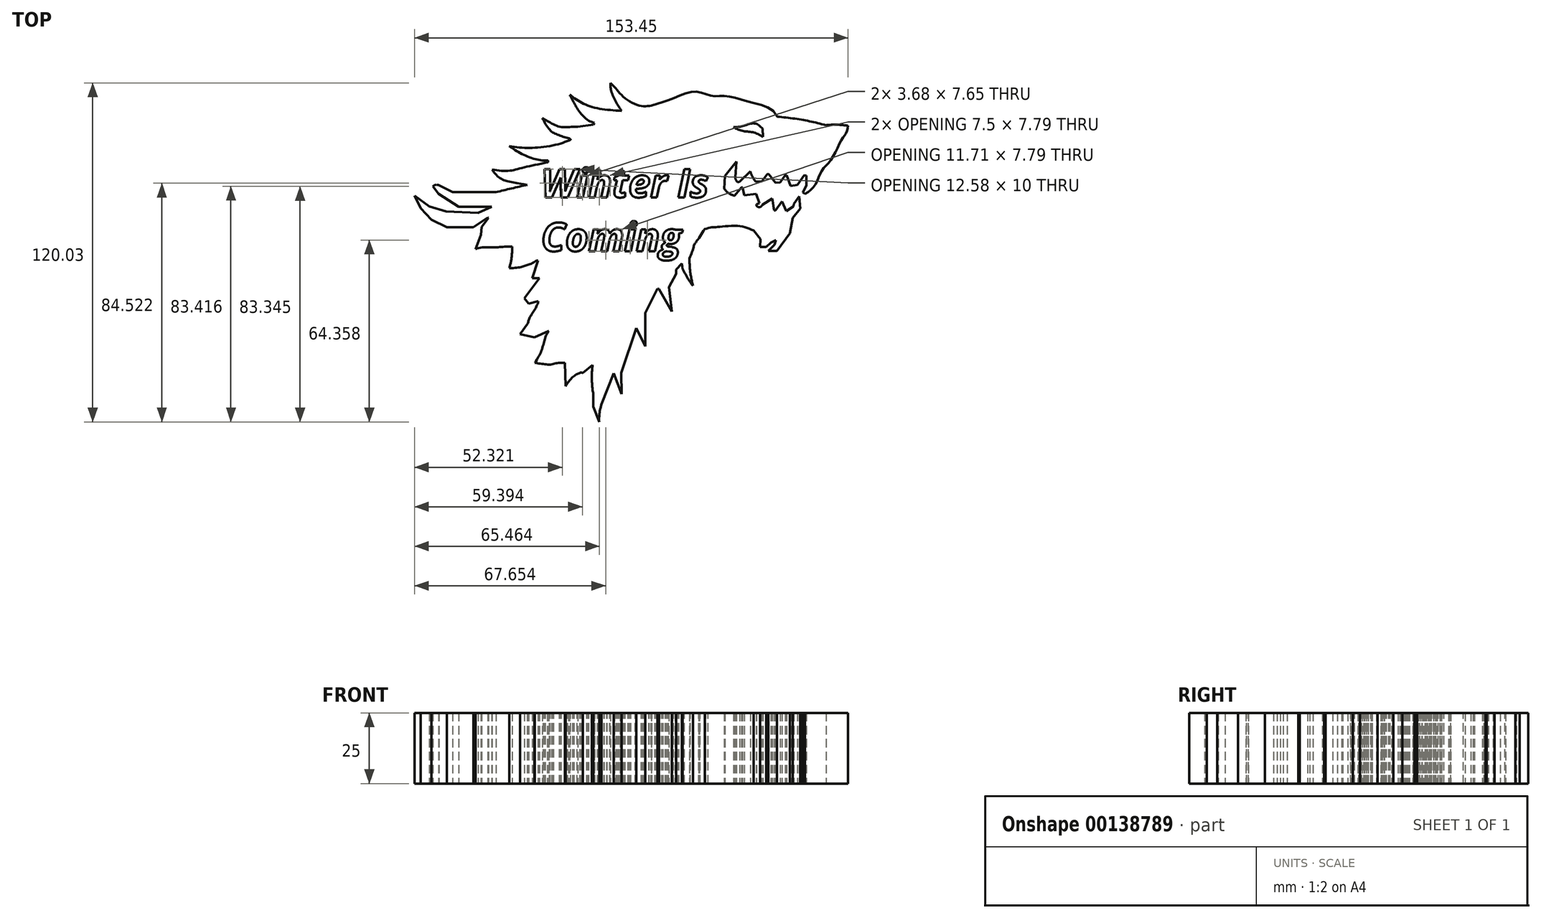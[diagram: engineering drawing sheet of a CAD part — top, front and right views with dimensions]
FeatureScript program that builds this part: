
annotation { "Feature Type Name" : "Feature", "Feature Type Description" : "" }
export const myFeature = defineFeature(function(context is Context, id is Id, definition is map)
    precondition{}
    {
        {
            var Q0;
            Q0=qCreatedBy(makeId("Top.planeOp"),FACE);
            var sketch = newSketch(context, id + "F0", { "sketchPlane" : qUnion([Q0])});
            skLineSegment(sketch, "E0", {"start": v(0, -46.34) * mm, "end": v(0, 97.64) * mm, "construction": true});
            skLineSegment(sketch, "E1", {"start": v(-98.9, 0) * mm, "end": v(160.67, 0) * mm, "construction": true});
            skFitSpline(sketch, "E2", {"points": [v(8.37, 46.02) * mm, v(16.5, 48.73) * mm, v(24.2, 50.9) * mm, v(29.67, 49.45) * mm, v(34.86, 49.36) * mm, v(43.4, 47.27) * mm, v(53, 42.06) * mm], "startDerivative": vector(47.53, 12.6) * mm, "endDerivative": vector(25.31, -53.78) * mm});
            skFitSpline(sketch, "E3", {"points": [v(53, 42.06) * mm, v(61.93, 40.92) * mm, v(70.2, 39.06) * mm], "startDerivative": vector(17.28, -1.4) * mm, "endDerivative": vector(17.12, -4.59) * mm});
            skFitSpline(sketch, "E4", {"points": [v(70.2, 39.06) * mm, v(73.91, 39.25) * mm, v(78, 38.88) * mm], "startDerivative": vector(7.53, 0.65) * mm, "endDerivative": vector(8.07, -1) * mm});
            skFitSpline(sketch, "E5", {"points": [v(78, 38.88) * mm, v(77.15, 36.05) * mm, v(75.57, 33.69) * mm, v(71.82, 26.58) * mm, v(68.71, 23.01) * mm, v(66.37, 17.92) * mm, v(62.79, 14.7) * mm], "startDerivative": vector(-2.44, -23.85) * mm, "endDerivative": vector(-25.04, -14.1) * mm});
            skLineSegment(sketch, "E6", {"start": v(62.79, 14.7) * mm, "end": v(62, 15.24) * mm});
            skLineSegment(sketch, "E7", {"start": v(62, 15.24) * mm, "end": v(63.2, 17.7) * mm});
            skLineSegment(sketch, "E8", {"start": v(63.2, 17.7) * mm, "end": v(63.2, 21.18) * mm});
            skLineSegment(sketch, "E9", {"start": v(63.2, 21.18) * mm, "end": v(62.45, 21.32) * mm});
            skLineSegment(sketch, "E10", {"start": v(62.45, 21.32) * mm, "end": v(60.09, 17.98) * mm});
            skLineSegment(sketch, "E11", {"start": v(60.09, 17.98) * mm, "end": v(57.72, 17.51) * mm});
            skLineSegment(sketch, "E12", {"start": v(57.72, 17.51) * mm, "end": v(56.32, 21.32) * mm});
            skLineSegment(sketch, "E13", {"start": v(56.32, 21.32) * mm, "end": v(55.78, 21.31) * mm});
            skLineSegment(sketch, "E14", {"start": v(55.78, 21.31) * mm, "end": v(54.02, 18.83) * mm});
            skLineSegment(sketch, "E15", {"start": v(54.02, 18.83) * mm, "end": v(52.38, 18.64) * mm});
            skLineSegment(sketch, "E16", {"start": v(52.38, 18.64) * mm, "end": v(49.96, 21.76) * mm});
            skLineSegment(sketch, "E17", {"start": v(49.96, 21.76) * mm, "end": v(49.36, 21.76) * mm});
            skLineSegment(sketch, "E18", {"start": v(49.36, 21.76) * mm, "end": v(47.55, 19.25) * mm});
            skLineSegment(sketch, "E19", {"start": v(47.55, 19.25) * mm, "end": v(45.5, 19.02) * mm});
            skFitSpline(sketch, "E20", {"points": [v(45.5, 19.02) * mm, v(44.43, 20.33) * mm, v(43.4, 22.76) * mm], "startDerivative": vector(-3.09, 1.68) * mm, "endDerivative": vector(-1.4, 5.58) * mm});
            skLineSegment(sketch, "E21", {"start": v(43.4, 22.76) * mm, "end": v(39.6, 19.05) * mm});
            skLineSegment(sketch, "E22", {"start": v(38.55, 26.15) * mm, "end": v(38.05, 20.53) * mm});
            skFitSpline(sketch, "E23", {"points": [v(38.05, 20.53) * mm, v(38.32, 19.7) * mm, v(38.9, 18.95) * mm, v(39.6, 19.05) * mm], "startDerivative": vector(0.59, -2.33) * mm, "endDerivative": vector(2.36, 0.9) * mm});
            skLineSegment(sketch, "E24", {"start": v(38.55, 26.15) * mm, "end": v(34.4, 21.11) * mm});
            skLineSegment(sketch, "E25", {"start": v(34.4, 21.11) * mm, "end": v(34.15, 16.58) * mm});
            skFitSpline(sketch, "E26", {"points": [v(34.15, 16.58) * mm, v(35.74, 14.98) * mm, v(37.83, 14.05) * mm], "startDerivative": vector(3.39, -3.5) * mm, "endDerivative": vector(3.98, -1.53) * mm});
            skLineSegment(sketch, "E27", {"start": v(37.83, 14.05) * mm, "end": v(40.2, 16.98) * mm});
            skLineSegment(sketch, "E28", {"start": v(40.2, 16.98) * mm, "end": v(40.7, 16.98) * mm});
            skLineSegment(sketch, "E29", {"start": v(40.7, 16.98) * mm, "end": v(41.3, 14.23) * mm});
            skLineSegment(sketch, "E30", {"start": v(41.3, 14.23) * mm, "end": v(45.53, 14.8) * mm});
            skLineSegment(sketch, "E31", {"start": v(45.53, 14.8) * mm, "end": v(46.61, 11.43) * mm});
            skLineSegment(sketch, "E32", {"start": v(46.61, 11.43) * mm, "end": v(45.6, 11.1) * mm});
            skLineSegment(sketch, "E33", {"start": v(47.71, 10.9) * mm, "end": v(51.18, 13.14) * mm});
            skFitSpline(sketch, "E34", {"points": [v(47.71, 10.9) * mm, v(47.14, 10.2) * mm, v(45.87, 10.24) * mm, v(45.6, 11.1) * mm], "startDerivative": vector(-1.25, -2.64) * mm, "endDerivative": vector(-0.16, 3.24) * mm});
            skLineSegment(sketch, "E35", {"start": v(51.18, 13.14) * mm, "end": v(51.76, 8.96) * mm});
            skLineSegment(sketch, "E36", {"start": v(51.76, 8.96) * mm, "end": v(52.35, 8.96) * mm});
            skLineSegment(sketch, "E37", {"start": v(52.35, 8.96) * mm, "end": v(54.64, 12.02) * mm});
            skLineSegment(sketch, "E38", {"start": v(54.64, 12.02) * mm, "end": v(56.15, 8.66) * mm});
            skLineSegment(sketch, "E39", {"start": v(56.15, 8.66) * mm, "end": v(58.7, 10.29) * mm});
            skLineSegment(sketch, "E40", {"start": v(58.7, 10.29) * mm, "end": v(58.8, 11.25) * mm});
            skLineSegment(sketch, "E41", {"start": v(58.8, 11.25) * mm, "end": v(60.75, 13.83) * mm});
            skLineSegment(sketch, "E42", {"start": v(60.75, 13.83) * mm, "end": v(61.12, 9.51) * mm});
            skLineSegment(sketch, "E43", {"start": v(61.12, 9.51) * mm, "end": v(58.37, 6.23) * mm});
            skLineSegment(sketch, "E44", {"start": v(58.37, 6.23) * mm, "end": v(57.38, 0.75) * mm});
            skLineSegment(sketch, "E45", {"start": v(57.38, 0.75) * mm, "end": v(52.78, -5.5) * mm});
            skLineSegment(sketch, "E46", {"start": v(52.78, -5.5) * mm, "end": v(49.73, -5.5) * mm});
            skLineSegment(sketch, "E47", {"start": v(49.73, -5.5) * mm, "end": v(52, -3.3) * mm});
            skLineSegment(sketch, "E48", {"start": v(52, -3.3) * mm, "end": v(52.42, -1.58) * mm});
            skLineSegment(sketch, "E49", {"start": v(52.42, -1.58) * mm, "end": v(50.65, -2.56) * mm});
            skLineSegment(sketch, "E50", {"start": v(50.65, -2.56) * mm, "end": v(49.07, -4.09) * mm});
            skLineSegment(sketch, "E51", {"start": v(49.07, -4.09) * mm, "end": v(46.86, -4.09) * mm});
            skLineSegment(sketch, "E52", {"start": v(46.86, -4.09) * mm, "end": v(47.02, -1.26) * mm});
            skLineSegment(sketch, "E53", {"start": v(47.02, -1.26) * mm, "end": v(44.6, 1.8) * mm});
            skFitSpline(sketch, "E54", {"points": [v(44.6, 1.8) * mm, v(38.62, 3.43) * mm, v(31.22, 2.96) * mm, v(30.22, 2.96) * mm, v(27.26, 2.3) * mm], "startDerivative": vector(-17, 7.19) * mm, "endDerivative": vector(-16.02, -4.1) * mm});
            skFitSpline(sketch, "E55", {"points": [v(27.26, 2.3) * mm, v(24.24, -2.27) * mm, v(23.71, -3.01) * mm, v(23.18, -4.49) * mm, v(21.86, -8.07) * mm], "startDerivative": vector(-9.48, -15.13) * mm, "endDerivative": vector(-7.44, -13.5) * mm});
            skFitSpline(sketch, "E56", {"points": [v(21.86, -8.07) * mm, v(22.1, -12.6) * mm, v(23.06, -17.73) * mm], "startDerivative": vector(0.3, -9.94) * mm, "endDerivative": vector(2.15, -9.73) * mm});
            skLineSegment(sketch, "E57", {"start": v(19.14, -9.9) * mm, "end": v(19.48, -11.87) * mm});
            skFitSpline(sketch, "E58", {"points": [v(19.48, -11.87) * mm, v(20.92, -14.56) * mm, v(23.06, -17.73) * mm], "startDerivative": vector(3.02, -5.51) * mm, "endDerivative": vector(4.86, -6.04) * mm});
            skLineSegment(sketch, "E59", {"start": v(19.14, -9.9) * mm, "end": v(17.18, -12.06) * mm});
            skLineSegment(sketch, "E60", {"start": v(17.18, -12.06) * mm, "end": v(17.18, -13.56) * mm});
            skLineSegment(sketch, "E61", {"start": v(17.18, -13.56) * mm, "end": v(14.64, -18.29) * mm});
            skLineSegment(sketch, "E62", {"start": v(14.64, -18.29) * mm, "end": v(15.58, -26.93) * mm});
            skLineSegment(sketch, "E63", {"start": v(15.58, -26.93) * mm, "end": v(11.12, -18.85) * mm});
            skLineSegment(sketch, "E64", {"start": v(11.12, -18.85) * mm, "end": v(10.6, -18.76) * mm});
            skLineSegment(sketch, "E65", {"start": v(10.6, -18.76) * mm, "end": v(6.22, -27.44) * mm});
            skLineSegment(sketch, "E66", {"start": v(6.22, -27.44) * mm, "end": v(6.17, -39.18) * mm});
            skLineSegment(sketch, "E67", {"start": v(6.17, -39.18) * mm, "end": v(3.07, -32.74) * mm});
            skLineSegment(sketch, "E68", {"start": v(3.07, -32.74) * mm, "end": v(-2.3, -48.66) * mm});
            skLineSegment(sketch, "E69", {"start": v(-2.3, -48.66) * mm, "end": v(-2.17, -56.06) * mm});
            skLineSegment(sketch, "E70", {"start": v(-2.17, -56.06) * mm, "end": v(-4.99, -48.79) * mm});
            skLineSegment(sketch, "E71", {"start": v(-4.99, -48.79) * mm, "end": v(-9.28, -59.71) * mm});
            skFitSpline(sketch, "E72", {"points": [v(-9.28, -59.71) * mm, v(-9.83, -61.89) * mm, v(-10.04, -63.68) * mm, v(-10.08, -65.99) * mm], "startDerivative": vector(-1.5, -7.23) * mm, "endDerivative": vector(0.61, -9.45) * mm});
            skLineSegment(sketch, "E73", {"start": v(-10.08, -65.99) * mm, "end": v(-12.22, -60.51) * mm});
            skLineSegment(sketch, "E74", {"start": v(-12.22, -60.51) * mm, "end": v(-12.22, -55.67) * mm});
            skFitSpline(sketch, "E75", {"points": [v(-12.22, -55.67) * mm, v(-12.62, -52.29) * mm, v(-12.62, -47.83) * mm, v(-12.44, -45.9) * mm], "startDerivative": vector(-2.35, 9.95) * mm, "endDerivative": vector(0.6, 6.7) * mm});
            skLineSegment(sketch, "E76", {"start": v(-12.44, -45.9) * mm, "end": v(-15.86, -48.6) * mm});
            skFitSpline(sketch, "E77", {"points": [v(-15.86, -48.6) * mm, v(-16.85, -48.6) * mm, v(-19.68, -50.34) * mm, v(-21.96, -53.33) * mm], "startDerivative": vector(-4.67, 0.75) * mm, "endDerivative": vector(-4.96, -8.28) * mm});
            skLineSegment(sketch, "E78", {"start": v(-21.96, -53.33) * mm, "end": v(-22.2, -45.03) * mm});
            skFitSpline(sketch, "E79", {"points": [v(-22.2, -45.03) * mm, v(-23.7, -45.03) * mm, v(-25.38, -45.24) * mm, v(-27.7, -45.69) * mm, v(-30.45, -45.39) * mm, v(-32.84, -45.03) * mm], "startDerivative": vector(-10.12, -0.25) * mm, "endDerivative": vector(-8.12, 2.64) * mm});
            skFitSpline(sketch, "E80", {"points": [v(-32.84, -45.03) * mm, v(-30.46, -40.57) * mm, v(-29.33, -36.68) * mm, v(-27.93, -33.79) * mm], "startDerivative": vector(7.96, 12) * mm, "endDerivative": vector(7.34, 9.15) * mm});
            skLineSegment(sketch, "E81", {"start": v(-27.93, -33.79) * mm, "end": v(-33, -36.1) * mm});
            skLineSegment(sketch, "E82", {"start": v(-33, -36.1) * mm, "end": v(-38.14, -34.9) * mm});
            skLineSegment(sketch, "E83", {"start": v(-38.14, -34.9) * mm, "end": v(-35.38, -31.25) * mm});
            skFitSpline(sketch, "E84", {"points": [v(-35.38, -31.25) * mm, v(-34.63, -29.02) * mm, v(-32.62, -25.74) * mm, v(-31.58, -23.28) * mm], "startDerivative": vector(1.7, 7.16) * mm, "endDerivative": vector(2.6, 7.43) * mm});
            skLineSegment(sketch, "E85", {"start": v(-31.58, -23.28) * mm, "end": v(-35.08, -24.1) * mm});
            skLineSegment(sketch, "E86", {"start": v(-35.08, -24.1) * mm, "end": v(-36.57, -22.16) * mm});
            skLineSegment(sketch, "E87", {"start": v(-36.57, -22.16) * mm, "end": v(-31.2, -15.15) * mm});
            skLineSegment(sketch, "E88", {"start": v(-31.2, -15.15) * mm, "end": v(-33.74, -15.15) * mm});
            skLineSegment(sketch, "E89", {"start": v(-33.74, -15.15) * mm, "end": v(-31.79, -8.9) * mm});
            skFitSpline(sketch, "E90", {"points": [v(-31.79, -8.9) * mm, v(-33.97, -9.91) * mm, v(-36.14, -10.62) * mm, v(-38.4, -11.28) * mm, v(-41.9, -11.6) * mm], "startDerivative": vector(-6.1, 1.36) * mm, "endDerivative": vector(-8.76, -0.8) * mm});
            skFitSpline(sketch, "E91", {"points": [v(-41.9, -11.6) * mm, v(-41.13, -8.29) * mm, v(-40.83, -3.95) * mm], "startDerivative": vector(1.85, 6.75) * mm, "endDerivative": vector(0.43, 8.1) * mm});
            skFitSpline(sketch, "E92", {"points": [v(-40.83, -3.95) * mm, v(-45.11, -4.06) * mm, v(-48.54, -4.17) * mm, v(-53.9, -4.78) * mm], "startDerivative": vector(-10.76, 1.27) * mm, "endDerivative": vector(-11.93, -6.43) * mm});
            skLineSegment(sketch, "E93", {"start": v(-53.9, -4.78) * mm, "end": v(-51.88, 0.27) * mm});
            skLineSegment(sketch, "E94", {"start": v(-51.88, 0.27) * mm, "end": v(-51.63, 3.08) * mm});
            skLineSegment(sketch, "E95", {"start": v(-51.63, 3.08) * mm, "end": v(-49.22, 6.21) * mm});
            skLineSegment(sketch, "E96", {"start": v(-49.22, 6.21) * mm, "end": v(-49.5, 6.43) * mm});
            skLineSegment(sketch, "E97", {"start": v(-49.5, 6.43) * mm, "end": v(-54.64, 2.98) * mm});
            skLineSegment(sketch, "E98", {"start": v(-54.64, 2.98) * mm, "end": v(-63.96, 2.98) * mm});
            skLineSegment(sketch, "E99", {"start": v(-63.96, 2.98) * mm, "end": v(-69.48, 5.65) * mm});
            skLineSegment(sketch, "E100", {"start": v(-69.48, 5.65) * mm, "end": v(-73.26, 9.73) * mm});
            skLineSegment(sketch, "E101", {"start": v(-73.26, 9.73) * mm, "end": v(-75.45, 14.1) * mm});
            skLineSegment(sketch, "E102", {"start": v(-75.45, 14.1) * mm, "end": v(-70.28, 10.27) * mm});
            skLineSegment(sketch, "E103", {"start": v(-70.28, 10.27) * mm, "end": v(-64.26, 8.53) * mm});
            skLineSegment(sketch, "E104", {"start": v(-64.26, 8.53) * mm, "end": v(-52.92, 7.99) * mm});
            skLineSegment(sketch, "E105", {"start": v(-52.92, 7.99) * mm, "end": v(-48.15, 10.22) * mm});
            skLineSegment(sketch, "E106", {"start": v(-48.15, 10.22) * mm, "end": v(-59.86, 10.22) * mm});
            skLineSegment(sketch, "E107", {"start": v(-59.86, 10.22) * mm, "end": v(-66.87, 14.75) * mm});
            skLineSegment(sketch, "E108", {"start": v(-66.87, 14.75) * mm, "end": v(-68.94, 17.44) * mm});
            skLineSegment(sketch, "E109", {"start": v(-66.8, 17.83) * mm, "end": v(-62.02, 15.35) * mm});
            skLineSegment(sketch, "E110", {"start": v(-62.02, 15.35) * mm, "end": v(-46.65, 15.35) * mm});
            skFitSpline(sketch, "E111", {"points": [v(-46.65, 15.35) * mm, v(-41.43, 16.6) * mm, v(-35.5, 17.98) * mm], "startDerivative": vector(10.61, 2.53) * mm, "endDerivative": vector(11.66, 2.74) * mm});
            skFitSpline(sketch, "E112", {"points": [v(-35.5, 17.98) * mm, v(-41.82, 19.11) * mm, v(-44.94, 20.17) * mm, v(-48, 23.3) * mm], "startDerivative": vector(-16.98, 1.76) * mm, "endDerivative": vector(-6.9, 10.96) * mm});
            skFitSpline(sketch, "E113", {"points": [v(-48, 23.3) * mm, v(-42.22, 22.9) * mm, v(-37.6, 23.9) * mm, v(-28.48, 25.89) * mm], "startDerivative": vector(19.28, -2.54) * mm, "endDerivative": vector(24.98, 5.08) * mm});
            skFitSpline(sketch, "E114", {"points": [v(-28.48, 26.58) * mm, v(-31.56, 26.78) * mm, v(-37.4, 28.87) * mm, v(-41.92, 31.66) * mm], "startDerivative": vector(-10.5, -0.18) * mm, "endDerivative": vector(-11.9, 8.2) * mm});
            skArc(sketch, "E115", {"start": v(-28.48, 25.89) * mm, "mid": v(-28.12, 26.23) * mm, "end": v(-28.48, 26.58) * mm});
            skFitSpline(sketch, "E116", {"points": [v(-68.94, 17.44) * mm, v(-67.92, 17.97) * mm, v(-66.8, 17.83) * mm], "startDerivative": vector(1.97, 1.4) * mm, "endDerivative": vector(2.31, -0.6) * mm});
            skFitSpline(sketch, "E117", {"points": [v(-41.92, 31.66) * mm, v(-36.84, 31.05) * mm, v(-31.36, 31.2) * mm, v(-24.7, 32.3) * mm, v(-20.72, 33.69) * mm], "startDerivative": vector(20.83, -3.13) * mm, "endDerivative": vector(16.42, 6.68) * mm});
            skFitSpline(sketch, "E118", {"points": [v(-20.72, 33.69) * mm, v(-20.23, 34.03) * mm, v(-20.92, 34.48) * mm], "startDerivative": vector(2.1, 0.45) * mm, "endDerivative": vector(-2.36, 1.12) * mm});
            skFitSpline(sketch, "E119", {"points": [v(-20.92, 34.48) * mm, v(-24.7, 35.66) * mm, v(-27.36, 37.18) * mm, v(-30.15, 41.53) * mm], "startDerivative": vector(-10.4, 0.84) * mm, "endDerivative": vector(-5.33, 11.62) * mm});
            skFitSpline(sketch, "E120", {"points": [v(-30.15, 41.53) * mm, v(-27.9, 40.27) * mm, v(-24.38, 38.58) * mm, v(-20.96, 38.41) * mm, v(-17.67, 38.48) * mm], "startDerivative": vector(9.55, -5.2) * mm, "endDerivative": vector(13.09, 0.11) * mm});
            skLineSegment(sketch, "E121", {"start": v(-17.67, 38.48) * mm, "end": v(-12.16, 39.28) * mm});
            skLineSegment(sketch, "E122", {"start": v(-12.16, 39.28) * mm, "end": v(-11.8, 39.9) * mm});
            skFitSpline(sketch, "E123", {"points": [v(-11.8, 39.9) * mm, v(-14.65, 41.23) * mm, v(-17.8, 44.9) * mm, v(-18.97, 46.96) * mm, v(-20.52, 49.83) * mm], "startDerivative": vector(-11.73, 3.62) * mm, "endDerivative": vector(-6.78, 12.4) * mm});
            skFitSpline(sketch, "E124", {"points": [v(-20.52, 49.83) * mm, v(-16.53, 47.15) * mm, v(-10.66, 45.04) * mm, v(-2.16, 44.15) * mm], "startDerivative": vector(13.1, -9.77) * mm, "endDerivative": vector(23.04, -1.36) * mm});
            skFitSpline(sketch, "E125", {"points": [v(-2.16, 44.15) * mm, v(-3.8, 46.7) * mm, v(-5.85, 51.28) * mm, v(-6.14, 54.04) * mm], "startDerivative": vector(-5.04, 7.36) * mm, "endDerivative": vector(-0.06, 8.63) * mm});
            skFitSpline(sketch, "E126", {"points": [v(-6.14, 54.04) * mm, v(-4.54, 52.44) * mm, v(-1.41, 49.01) * mm, v(4.44, 45.88) * mm, v(8.37, 46.02) * mm], "startDerivative": vector(8.45, -7.78) * mm, "endDerivative": vector(15.33, 2.76) * mm});
            skFitSpline(sketch, "E127", {"points": [v(37.42, 38.31) * mm, v(40.78, 37) * mm, v(44.4, 36.52) * mm, v(47.82, 34.96) * mm], "startDerivative": vector(9.91, -4.83) * mm, "endDerivative": vector(9.8, -5.8) * mm});
            skFitSpline(sketch, "E128", {"points": [v(37.42, 38.31) * mm, v(40.89, 38.8) * mm, v(43.76, 39.66) * mm, v(46.07, 39.28) * mm, v(47.7, 37.83) * mm], "startDerivative": vector(15.86, 1.57) * mm, "endDerivative": vector(4.95, -5.03) * mm});
            skLineSegment(sketch, "E129", {"start": v(47.7, 37.83) * mm, "end": v(47.82, 34.96) * mm});
            skSolve(sketch);
        }
        {
            var Q0;
            Q0=makeQuery(id+"F0.imprint","IMPRINT",FACE,{"disambiguationData":[TD([[makeQuery(id+"F0.imprint","IMPRINT",EDGE,{"derivedFrom":sQuery(id+"F0.wireOp",EDGE,"E2")}),-1.0]])]});
            extrude(context, id + "F1", {"entities" : qUnion([Q0]), "depth" : 25 * mm});
        }
        {
            var Q0;
            Q0=qCreatedBy(makeId("Top.planeOp"),FACE);
            var sketch = newSketch(context, id + "F2", { "sketchPlane" : qUnion([Q0])});
            skCircle(sketch, "E130", {"center": v(0, 0) * mm, "radius": 94.35 * mm});
            skEllipse(sketch, "E131", {"center": v(0, 81.58) * mm, "majorRadius": 14.76 * mm, "minorRadius": 7.47 * mm, "majorAxis": v(1, 0)});
            skSolve(sketch);
        }
        {
            var Q0;
            Q0=makeQuery(id+"F2.imprint","IMPRINT",FACE,{"disambiguationData":[TD([[makeQuery(id+"F2.imprint","IMPRINT",EDGE,{"derivedFrom":sQuery(id+"F2.wireOp",EDGE,"E130")}),1.0]])]});
            extrude(context, id + "F3", {"entities" : qUnion([Q0]), "depth" : 25 * mm});
        }
        {
            var Q0;
            Q0=makeQuery(id+"F3.opExtrude","SWEPT_BODY",BODY,{"disambiguationData":[OSD([sQuery(id+"F2.wireOp",EDGE,"E130"),sQuery(id+"F2.wireOp",EDGE,"E131")])]});
            deleteBodies(context, id + "F4", {"entities" : qUnion([Q0])});
        }
        {
            var Q0;
            Q0=makeQuery(id+"F1.opExtrude","CAP_FACE",FACE,{"disambiguationData":[OSD([sQuery(id+"F0.wireOp",EDGE,"E2"),sQuery(id+"F0.wireOp",EDGE,"E3"),sQuery(id+"F0.wireOp",EDGE,"E4"),sQuery(id+"F0.wireOp",EDGE,"E5"),sQuery(id+"F0.wireOp",EDGE,"E6"),sQuery(id+"F0.wireOp",EDGE,"E7"),sQuery(id+"F0.wireOp",EDGE,"E8"),sQuery(id+"F0.wireOp",EDGE,"E9"),sQuery(id+"F0.wireOp",EDGE,"E10"),sQuery(id+"F0.wireOp",EDGE,"E11"),sQuery(id+"F0.wireOp",EDGE,"E12"),sQuery(id+"F0.wireOp",EDGE,"E13"),sQuery(id+"F0.wireOp",EDGE,"E14"),sQuery(id+"F0.wireOp",EDGE,"E15"),sQuery(id+"F0.wireOp",EDGE,"E16"),sQuery(id+"F0.wireOp",EDGE,"E17"),sQuery(id+"F0.wireOp",EDGE,"E18"),sQuery(id+"F0.wireOp",EDGE,"E19"),sQuery(id+"F0.wireOp",EDGE,"E20"),sQuery(id+"F0.wireOp",EDGE,"E21"),sQuery(id+"F0.wireOp",EDGE,"E22"),sQuery(id+"F0.wireOp",EDGE,"E23"),sQuery(id+"F0.wireOp",EDGE,"E24"),sQuery(id+"F0.wireOp",EDGE,"E25"),sQuery(id+"F0.wireOp",EDGE,"E26"),sQuery(id+"F0.wireOp",EDGE,"E27"),sQuery(id+"F0.wireOp",EDGE,"E28"),sQuery(id+"F0.wireOp",EDGE,"E29"),sQuery(id+"F0.wireOp",EDGE,"E30"),sQuery(id+"F0.wireOp",EDGE,"E31"),sQuery(id+"F0.wireOp",EDGE,"E32"),sQuery(id+"F0.wireOp",EDGE,"E33"),sQuery(id+"F0.wireOp",EDGE,"E34"),sQuery(id+"F0.wireOp",EDGE,"E35"),sQuery(id+"F0.wireOp",EDGE,"E36"),sQuery(id+"F0.wireOp",EDGE,"E37"),sQuery(id+"F0.wireOp",EDGE,"E38"),sQuery(id+"F0.wireOp",EDGE,"E39"),sQuery(id+"F0.wireOp",EDGE,"E40"),sQuery(id+"F0.wireOp",EDGE,"E41"),sQuery(id+"F0.wireOp",EDGE,"E42"),sQuery(id+"F0.wireOp",EDGE,"E43"),sQuery(id+"F0.wireOp",EDGE,"E44"),sQuery(id+"F0.wireOp",EDGE,"E45"),sQuery(id+"F0.wireOp",EDGE,"E46"),sQuery(id+"F0.wireOp",EDGE,"E47"),sQuery(id+"F0.wireOp",EDGE,"E48"),sQuery(id+"F0.wireOp",EDGE,"E49"),sQuery(id+"F0.wireOp",EDGE,"E50"),sQuery(id+"F0.wireOp",EDGE,"E51"),sQuery(id+"F0.wireOp",EDGE,"E52"),sQuery(id+"F0.wireOp",EDGE,"E53"),sQuery(id+"F0.wireOp",EDGE,"E54"),sQuery(id+"F0.wireOp",EDGE,"E55"),sQuery(id+"F0.wireOp",EDGE,"E56"),sQuery(id+"F0.wireOp",EDGE,"E57"),sQuery(id+"F0.wireOp",EDGE,"E58"),sQuery(id+"F0.wireOp",EDGE,"E59"),sQuery(id+"F0.wireOp",EDGE,"E60"),sQuery(id+"F0.wireOp",EDGE,"E61"),sQuery(id+"F0.wireOp",EDGE,"E62"),sQuery(id+"F0.wireOp",EDGE,"E63"),sQuery(id+"F0.wireOp",EDGE,"E64"),sQuery(id+"F0.wireOp",EDGE,"E65"),sQuery(id+"F0.wireOp",EDGE,"E66"),sQuery(id+"F0.wireOp",EDGE,"E67"),sQuery(id+"F0.wireOp",EDGE,"E68"),sQuery(id+"F0.wireOp",EDGE,"E69"),sQuery(id+"F0.wireOp",EDGE,"E70"),sQuery(id+"F0.wireOp",EDGE,"E71"),sQuery(id+"F0.wireOp",EDGE,"E72"),sQuery(id+"F0.wireOp",EDGE,"E73"),sQuery(id+"F0.wireOp",EDGE,"E74"),sQuery(id+"F0.wireOp",EDGE,"E75"),sQuery(id+"F0.wireOp",EDGE,"E76"),sQuery(id+"F0.wireOp",EDGE,"E77"),sQuery(id+"F0.wireOp",EDGE,"E78"),sQuery(id+"F0.wireOp",EDGE,"E79"),sQuery(id+"F0.wireOp",EDGE,"E80"),sQuery(id+"F0.wireOp",EDGE,"E81"),sQuery(id+"F0.wireOp",EDGE,"E82"),sQuery(id+"F0.wireOp",EDGE,"E83"),sQuery(id+"F0.wireOp",EDGE,"E84"),sQuery(id+"F0.wireOp",EDGE,"E85"),sQuery(id+"F0.wireOp",EDGE,"E86"),sQuery(id+"F0.wireOp",EDGE,"E87"),sQuery(id+"F0.wireOp",EDGE,"E88"),sQuery(id+"F0.wireOp",EDGE,"E89"),sQuery(id+"F0.wireOp",EDGE,"E90"),sQuery(id+"F0.wireOp",EDGE,"E91"),sQuery(id+"F0.wireOp",EDGE,"E92"),sQuery(id+"F0.wireOp",EDGE,"E93"),sQuery(id+"F0.wireOp",EDGE,"E94"),sQuery(id+"F0.wireOp",EDGE,"E95"),sQuery(id+"F0.wireOp",EDGE,"E96"),sQuery(id+"F0.wireOp",EDGE,"E97"),sQuery(id+"F0.wireOp",EDGE,"E98"),sQuery(id+"F0.wireOp",EDGE,"E99"),sQuery(id+"F0.wireOp",EDGE,"E100"),sQuery(id+"F0.wireOp",EDGE,"E101"),sQuery(id+"F0.wireOp",EDGE,"E102"),sQuery(id+"F0.wireOp",EDGE,"E103"),sQuery(id+"F0.wireOp",EDGE,"E104"),sQuery(id+"F0.wireOp",EDGE,"E105"),sQuery(id+"F0.wireOp",EDGE,"E106"),sQuery(id+"F0.wireOp",EDGE,"E107"),sQuery(id+"F0.wireOp",EDGE,"E108"),sQuery(id+"F0.wireOp",EDGE,"E109"),sQuery(id+"F0.wireOp",EDGE,"E110"),sQuery(id+"F0.wireOp",EDGE,"E111"),sQuery(id+"F0.wireOp",EDGE,"E112"),sQuery(id+"F0.wireOp",EDGE,"E113"),sQuery(id+"F0.wireOp",EDGE,"E114"),sQuery(id+"F0.wireOp",EDGE,"E115"),sQuery(id+"F0.wireOp",EDGE,"E116"),sQuery(id+"F0.wireOp",EDGE,"E117"),sQuery(id+"F0.wireOp",EDGE,"E118"),sQuery(id+"F0.wireOp",EDGE,"E119"),sQuery(id+"F0.wireOp",EDGE,"E120"),sQuery(id+"F0.wireOp",EDGE,"E121"),sQuery(id+"F0.wireOp",EDGE,"E122"),sQuery(id+"F0.wireOp",EDGE,"E123"),sQuery(id+"F0.wireOp",EDGE,"E124"),sQuery(id+"F0.wireOp",EDGE,"E125"),sQuery(id+"F0.wireOp",EDGE,"E126"),sQuery(id+"F0.wireOp",EDGE,"E127"),sQuery(id+"F0.wireOp",EDGE,"E128"),sQuery(id+"F0.wireOp",EDGE,"E129")])],"isStart":false});
            var sketch = newSketch(context, id + "F5", { "sketchPlane" : qUnion([Q0])});
            skText(sketch, "E132", { "text": "Winter Is\nComing", "fontName": "OpenSans-BoldItalic.ttf"});
            const initialGuessF5  = {"E132": [-0.03068, 0.01353, 1, 0, 0.01009]};
            skSetInitialGuess(sketch, initialGuessF5);
            skSolve(sketch);
        }
        {
            var Q0;
            Q0 = qSketchRegion(id + "F5", true);
            extrude(context, id + "F6", {"entities" : qUnion([Q0]), "operationType" : NewBodyOperationType.REMOVE, "oppositeDirection" : true, "depth" : 25 * mm});
        }
    });
